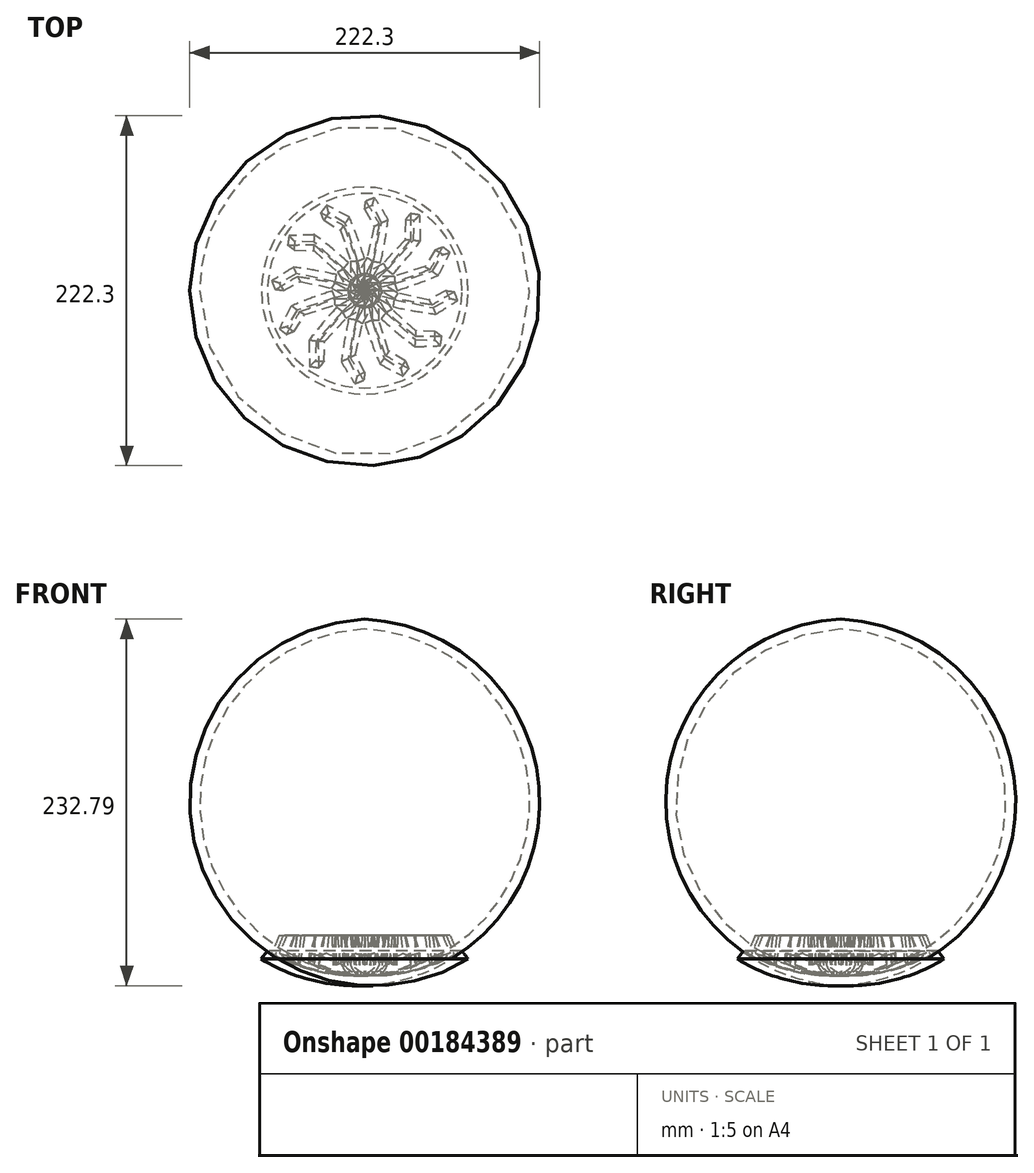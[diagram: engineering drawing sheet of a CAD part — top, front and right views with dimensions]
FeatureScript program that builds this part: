
annotation { "Feature Type Name" : "Feature", "Feature Type Description" : "" }
export const myFeature = defineFeature(function(context is Context, id is Id, definition is map)
    precondition{}
    {
        {
            var Q0;
            Q0=qCreatedBy(makeId("Top.planeOp"),FACE);
            var sketch = newSketch(context, id + "F0", { "sketchPlane" : qUnion([Q0])});
            skLineSegment(sketch, "E0", {"start": v(0, 0) * mm, "end": v(20.65, 0) * mm});
            skLineSegment(sketch, "E1", {"start": v(20.65, 0) * mm, "end": v(49.27, 8.36) * mm});
            skLineSegment(sketch, "E2", {"start": v(49.27, 8.36) * mm, "end": v(60.42, 26.03) * mm});
            skLineSegment(sketch, "E3", {"start": v(60.42, 26.03) * mm, "end": v(53.12, 28.72) * mm});
            skLineSegment(sketch, "E4", {"start": v(53.12, 28.72) * mm, "end": v(42.92, 12.54) * mm});
            skLineSegment(sketch, "E5", {"start": v(42.92, 12.54) * mm, "end": v(18.73, 4.9) * mm});
            skLineSegment(sketch, "E6", {"start": v(18.73, 4.9) * mm, "end": v(0, 4.9) * mm});
            skLineSegment(sketch, "E7", {"start": v(0, 4.9) * mm, "end": v(0, 0) * mm});
            skSolve(sketch);
        }
        {
            var Q0;
            Q0=qCreatedBy(makeId("Top.planeOp"),FACE);
            cPlane(context, id + "F1", {"entities" : qUnion([Q0]), "cplaneType" : CPlaneType.OFFSET, "offset" : 12.7 * mm, "width" : 152.4 * mm, "height" : 152.4 * mm});
        }
        {
            var Q0;
            Q0=qCreatedBy(id+"F1.planeOp",FACE);
            cPlane(context, id + "F2", {"entities" : qUnion([Q0]), "cplaneType" : CPlaneType.OFFSET, "offset" : 12.7 * mm, "width" : 152.4 * mm, "height" : 152.4 * mm});
        }
        {
            var Q0;
            Q0=qCreatedBy(id+"F1.planeOp",FACE);
            var sketch = newSketch(context, id + "F3", { "sketchPlane" : qUnion([Q0])});
            skLineSegment(sketch, "E8", {"start": v(0, 0) * mm, "end": v(19.88, 2.02) * mm});
            skLineSegment(sketch, "E9", {"start": v(19.88, 2.02) * mm, "end": v(45.43, 10.47) * mm});
            skLineSegment(sketch, "E10", {"start": v(45.43, 10.47) * mm, "end": v(54.84, 24.3) * mm});
            skLineSegment(sketch, "E11", {"start": v(54.84, 24.3) * mm, "end": v(49.61, 27.86) * mm});
            skLineSegment(sketch, "E12", {"start": v(49.61, 27.86) * mm, "end": v(40.25, 14.1) * mm});
            skLineSegment(sketch, "E13", {"start": v(40.25, 14.1) * mm, "end": v(18.92, 7.59) * mm});
            skLineSegment(sketch, "E14", {"start": v(18.92, 7.59) * mm, "end": v(0, 7.59) * mm});
            skLineSegment(sketch, "E15", {"start": v(0, 7.59) * mm, "end": v(0, 0) * mm});
            skSolve(sketch);
        }
        {
            var Q0;
            Q0=qCreatedBy(id+"F2.planeOp",FACE);
            var sketch = newSketch(context, id + "F4", { "sketchPlane" : qUnion([Q0])});
            skLineSegment(sketch, "E16", {"start": v(0, 0) * mm, "end": v(18.92, 4.51) * mm});
            skLineSegment(sketch, "E17", {"start": v(18.92, 4.51) * mm, "end": v(42.93, 12.4) * mm});
            skLineSegment(sketch, "E18", {"start": v(42.93, 12.4) * mm, "end": v(49.47, 22.96) * mm});
            skLineSegment(sketch, "E19", {"start": v(49.47, 22.96) * mm, "end": v(44.77, 25.86) * mm});
            skLineSegment(sketch, "E20", {"start": v(44.77, 25.86) * mm, "end": v(38.2, 15.23) * mm});
            skLineSegment(sketch, "E21", {"start": v(38.2, 15.23) * mm, "end": v(18.92, 9.12) * mm});
            skLineSegment(sketch, "E22", {"start": v(18.92, 9.12) * mm, "end": v(0, 9.12) * mm});
            skLineSegment(sketch, "E23", {"start": v(0, 9.12) * mm, "end": v(0, 0) * mm});
            skSolve(sketch);
        }
        {
            var Q0;
            Q0=makeQuery(id+"F4.imprint","IMPRINT",FACE,{"disambiguationData":[TD([[makeQuery(id+"F4.imprint","IMPRINT",EDGE,{"derivedFrom":sQuery(id+"F4.wireOp",EDGE,"E16")}),1.0]])]});
            var Q1;
            Q1=makeQuery(id+"F3.imprint","IMPRINT",FACE,{"disambiguationData":[TD([[makeQuery(id+"F3.imprint","IMPRINT",EDGE,{"derivedFrom":sQuery(id+"F3.wireOp",EDGE,"E8")}),1.0]])]});
            var Q2;
            Q2=makeQuery(id+"F0.imprint","IMPRINT",FACE,{"disambiguationData":[TD([[makeQuery(id+"F0.imprint","IMPRINT",EDGE,{"derivedFrom":sQuery(id+"F0.wireOp",EDGE,"E0")}),1.0]])]});
            loft(context, id + "F5", {"sheetProfilesArray" : [{ "sheetProfileEntities" : qUnion([Q0]) }, { "sheetProfileEntities" : qUnion([Q1]) }, { "sheetProfileEntities" : qUnion([Q2]) }]});
        }
        {
            var Q0;
            Q0=makeQuery(id+"F5.opLoft","SWEPT_BODY",BODY,{"disambiguationData":[OSD([makeQuery(id+"F0.imprint","IMPRINT",FACE,{"disambiguationData":[TD([[makeQuery(id+"F0.imprint","IMPRINT",EDGE,{"derivedFrom":sQuery(id+"F0.wireOp",EDGE,"E0")}),1.0]])]}),sQuery(id+"F3.wireOp",EDGE,"E13"),makeQuery(id+"F4.imprint","IMPRINT",FACE,{"disambiguationData":[TD([[makeQuery(id+"F4.imprint","IMPRINT",EDGE,{"derivedFrom":sQuery(id+"F4.wireOp",EDGE,"E16")}),1.0]])]})])]});
            var Q1;
            Q1=makeQuery(id+"F5.opLoft","SWEPT_EDGE",EDGE,{"disambiguationData":[OSD([sQuery(id+"F3.wireOp",EDGE,"E8"),sQuery(id+"F3.wireOp",EDGE,"E15"),sQuery(id+"F4.wireOp",EDGE,"E16"),sQuery(id+"F4.wireOp",EDGE,"E23")])]});
            circularPattern(context, id + "F6", {"entities" : qUnion([Q0]), "axis" : qUnion([Q1]), "angle" : 30 * degree, "instanceCount" : 12});
        }
        {
            var Q0;
            Q0=qCreatedBy(makeId("Front.planeOp"),FACE);
            var sketch = newSketch(context, id + "F7", { "sketchPlane" : qUnion([Q0])});
            skArc(sketch, "E24", {"start": v(0, 0) * mm, "mid": v(40.3, 5.58) * mm, "end": v(75.83, 25.43) * mm});
            skLineSegment(sketch, "E25", {"start": v(75.83, 25.43) * mm, "end": v(0, 25.43) * mm});
            skLineSegment(sketch, "E26", {"start": v(0, 25.43) * mm, "end": v(0, 0) * mm});
            skSolve(sketch);
        }
        {
            var Q0;
            Q0=qCreatedBy(makeId("Front.planeOp"),FACE);
            var sketch = newSketch(context, id + "F8", { "sketchPlane" : qUnion([Q0])});
            skLineSegment(sketch, "E27", {"start": v(0, 37.23) * mm, "end": v(0, -23.7) * mm});
            skSolve(sketch);
        }
        {
            var Q0;
            Q0=makeQuery(id+"F7.imprint","IMPRINT",FACE,{"disambiguationData":[TD([[makeQuery(id+"F7.imprint","IMPRINT",EDGE,{"derivedFrom":sQuery(id+"F7.wireOp",EDGE,"E24")}),1.0]])]});
            var Q1;
            Q1=sQuery(id+"F8.wireOp",EDGE,"E27");
            revolve(context, id + "F9", {"operationType" : NewBodyOperationType.INTERSECT, "entities" : qUnion([Q0]), "axis" : qUnion([Q1]), "revolveType" : RevolveType.FULL, "oppositeDirection" : true});
        }
        {
            var Q0;
            Q0=qCreatedBy(makeId("Front.planeOp"),FACE);
            var sketch = newSketch(context, id + "F10", { "sketchPlane" : qUnion([Q0])});
            skArc(sketch, "E28.0", {"start": v(0, 0) * mm, "mid": v(32.04, 3.17) * mm, "end": v(61.8, 15.47) * mm});
            skArc(sketch, "E29.0", {"start": v(0, -6.36) * mm, "mid": v(34.1, -2.86) * mm, "end": v(65.7, 10.4) * mm});
            skLineSegment(sketch, "E30", {"start": v(0, 0) * mm, "end": v(0, -6.36) * mm});
            skPoint(sketch, "E31.start.orphan", {"position": v(75.83, 25.43) * mm});
            skLineSegment(sketch, "E32", {"start": v(61.8, 15.47) * mm, "end": v(65.7, 10.4) * mm});
            skSolve(sketch);
        }
        {
            var Q0;
            Q0=makeQuery(id+"F10.imprint","IMPRINT",FACE,{"disambiguationData":[TD([[makeQuery(id+"F10.imprint","IMPRINT",EDGE,{"derivedFrom":sQuery(id+"F10.wireOp",EDGE,"E28.0")}),-1.0]])]});
            var Q1;
            Q1=sQuery(id+"F8.wireOp",EDGE,"E27");
            revolve(context, id + "F11", {"entities" : qUnion([Q0]), "axis" : qUnion([Q1]), "revolveType" : RevolveType.FULL});
        }
    });
